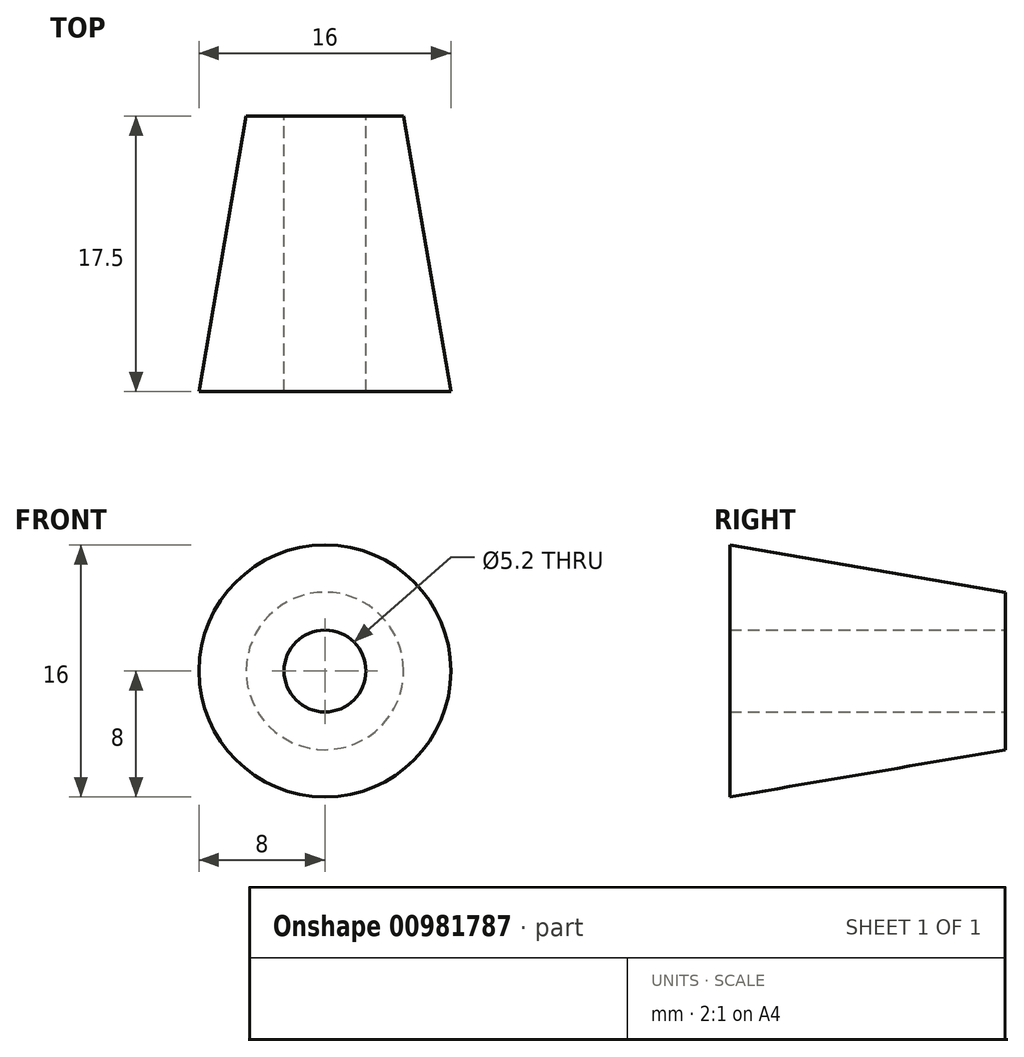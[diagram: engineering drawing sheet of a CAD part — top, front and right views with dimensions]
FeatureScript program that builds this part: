
annotation { "Feature Type Name" : "Feature", "Feature Type Description" : "" }
export const myFeature = defineFeature(function(context is Context, id is Id, definition is map)
    precondition{}
    {
        {
            var Q0;
            Q0=qCreatedBy(makeId("Front.planeOp"),FACE);
            var sketch = newSketch(context, id + "F0", { "sketchPlane" : qUnion([Q0])});
            skCircle(sketch, "E0", {"center": v(0, 0) * mm, "radius": 5 * mm});
            skLineSegment(sketch, "E1", {"start": v(0, 0) * mm, "end": v(0, -5) * mm});
            skSolve(sketch);
        }
        {
            var Q0;
            Q0=qCreatedBy(makeId("Front.planeOp"),FACE);
            cPlane(context, id + "F1", {"entities" : qUnion([Q0]), "cplaneType" : CPlaneType.OFFSET, "offset" : 17.5 * mm, "width" : 150 * mm, "height" : 150 * mm});
        }
        {
            var Q0;
            Q0=qCreatedBy(id+"F1.planeOp",FACE);
            var sketch = newSketch(context, id + "F2", { "sketchPlane" : qUnion([Q0])});
            skCircle(sketch, "E2", {"center": v(0, 0) * mm, "radius": 8 * mm});
            skSolve(sketch);
        }
        {
            var Q0;
            Q0=makeQuery(id+"F2.imprint","IMPRINT",FACE,{"disambiguationData":[TD([[makeQuery(id+"F2.imprint","IMPRINT",EDGE,{"derivedFrom":sQuery(id+"F2.wireOp",EDGE,"E2")}),1.0]])]});
            var Q1;
            Q1=makeQuery(id+"F0.imprint","IMPRINT",FACE,{"disambiguationData":[TD([[makeQuery(id+"F0.imprint","IMPRINT",EDGE,{"derivedFrom":sQuery(id+"F0.wireOp",EDGE,"E0")}),1.0]])]});
            loft(context, id + "F3", {"sheetProfilesArray" : [{ "sheetProfileEntities" : qUnion([Q0]) }, { "sheetProfileEntities" : qUnion([Q1]) }]});
        }
        {
            var Q0;
            Q0=sQuery(id+"F0.wireOp",VERTEX,"E1.start");
            var Q1;
            Q1=makeQuery(id+"F3.opLoft","SWEPT_BODY",BODY,{"disambiguationData":[OSD([makeQuery(id+"F0.imprint","IMPRINT",FACE,{"disambiguationData":[TD([[makeQuery(id+"F0.imprint","IMPRINT",EDGE,{"derivedFrom":sQuery(id+"F0.wireOp",EDGE,"E0")}),1.0]])]}),makeQuery(id+"F2.imprint","IMPRINT",FACE,{"disambiguationData":[TD([[makeQuery(id+"F2.imprint","IMPRINT",EDGE,{"derivedFrom":sQuery(id+"F2.wireOp",EDGE,"E2")}),1.0]])]})])]});
            hole(context, id + "F4", {"style" : HoleStyle.SIMPLE, "endStyle" : HoleEndStyle.THROUGH, "oppositeDirection" : true, "holeDiameter" : 5.2 * mm, "majorDiameter" : 5 * mm, "isTappedThrough" : true, "tappedDepth" : 12 * mm, "tapClearance" : 3, "locations" : qUnion([Q0]), "scope" : qUnion([Q1])});
        }
    });
